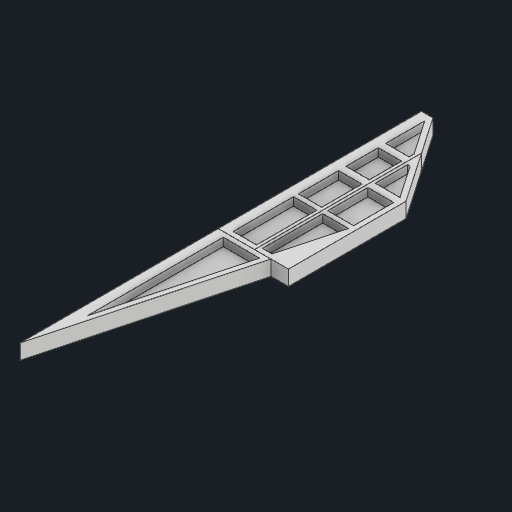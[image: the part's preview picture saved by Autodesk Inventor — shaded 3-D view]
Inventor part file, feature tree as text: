
AUTODESK INVENTOR PART (.ipt)
format: ipt  version: 2024 (Build 280153000, 153)  size: 308,224 bytes
history: native  units: in
note: dims shown in document units (in); Inventor stores cm internally (conversion verified against a paired STEP export)
features: other x3, sketch x2
ambient origin geometry x8: Origin, YZ Plane, XZ Plane, XY Plane, X Axis, Y Axis, Z Axis, Center Point
bodies: Solid1 (feature_tree)
feature tree (5):
  other  "Nozki.ipt"
  other  "Solid1::Nozki.ipt"
  other  "TaggingFeature1"
  sketch  "Sketch1"  dims[d0=0.3937in]
  sketch  "Sketch2"
